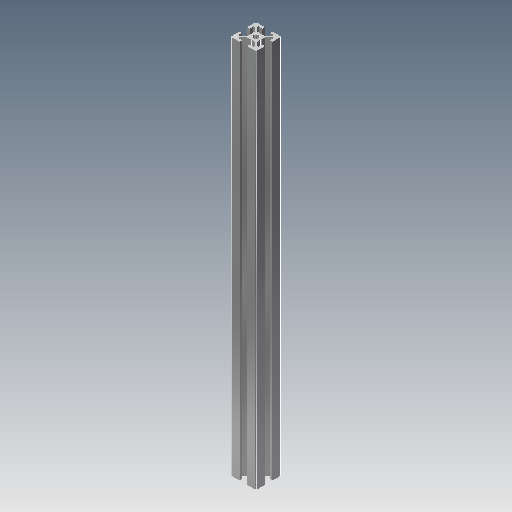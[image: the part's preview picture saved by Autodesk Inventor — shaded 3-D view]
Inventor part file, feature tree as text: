
AUTODESK INVENTOR PART (.ipt)
format: ipt  version: 2018 (Build 220112000, 112)  size: 161,792 bytes
history: native  units: mm
features: other x1, extrude x1, sketch x1
ambient origin geometry x8: Origin, YZ Plane, XZ Plane, XY Plane, X Axis, Y Axis, Z Axis, Center Point
bodies: Solid1 (feature_tree)
feature tree (3):
  other  "<userpath>\OneDrive\projects\sPhenixTileTestStand\sPhenixTileTestStand.xlsx"
  extrude  "Extrusion1"  [1 undecoded]
  sketch  "Sketch1"  dims[d0=300.0mm d1=0.0mm]
note: 1 required parameter value undecoded (feature->parameter linkage not recoverable at this tier; creation-order binding heuristic only, values carry confidence <= 0.55)
